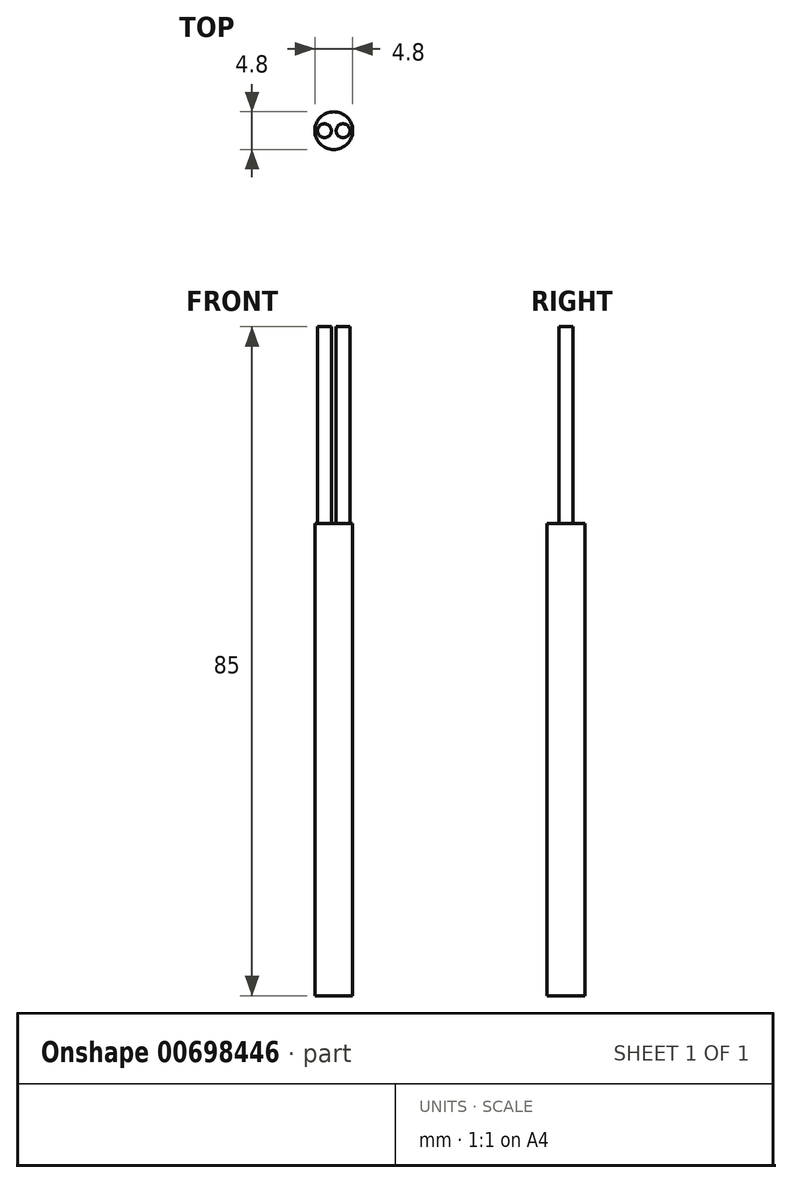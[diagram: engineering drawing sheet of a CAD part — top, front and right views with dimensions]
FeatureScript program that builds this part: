
annotation { "Feature Type Name" : "Feature", "Feature Type Description" : "" }
export const myFeature = defineFeature(function(context is Context, id is Id, definition is map)
    precondition{}
    {
        {
            var Q0;
            Q0=qCreatedBy(makeId("Top.planeOp"),FACE);
            var sketch = newSketch(context, id + "F0", { "sketchPlane" : qUnion([Q0])});
            skCircle(sketch, "E0", {"center": v(0, 0) * mm, "radius": 2.4 * mm});
            skSolve(sketch);
        }
        {
            var Q0;
            Q0 = qSketchRegion(id + "F0", true);
            extrude(context, id + "F1", {"entities" : qUnion([Q0]), "depth" : 60 * mm, "offsetDistance" : 25 * mm});
        }
        {
            var Q0;
            Q0=makeQuery(id+"F1.opExtrude","CAP_FACE",FACE,{"disambiguationData":[OSD([sQuery(id+"F0.wireOp",EDGE,"E0")])],"isStart":false});
            var sketch = newSketch(context, id + "F2", { "sketchPlane" : qUnion([Q0])});
            skCircle(sketch, "E1", {"center": v(-1.18, 0) * mm, "radius": 0.87 * mm});
            skLineSegment(sketch, "E2", {"start": v(0, 0) * mm, "end": v(0, 0.57) * mm});
            skCircle(sketch, "E3.MirrorC", {"center": v(1.18, 0) * mm, "radius": 0.87 * mm});
            skSolve(sketch);
        }
        {
            var Q0;
            Q0 = qSketchRegion(id + "F2", true);
            extrude(context, id + "F3", {"entities" : qUnion([Q0]), "operationType" : NewBodyOperationType.ADD, "depth" : 25 * mm, "offsetDistance" : 25 * mm});
        }
    });
